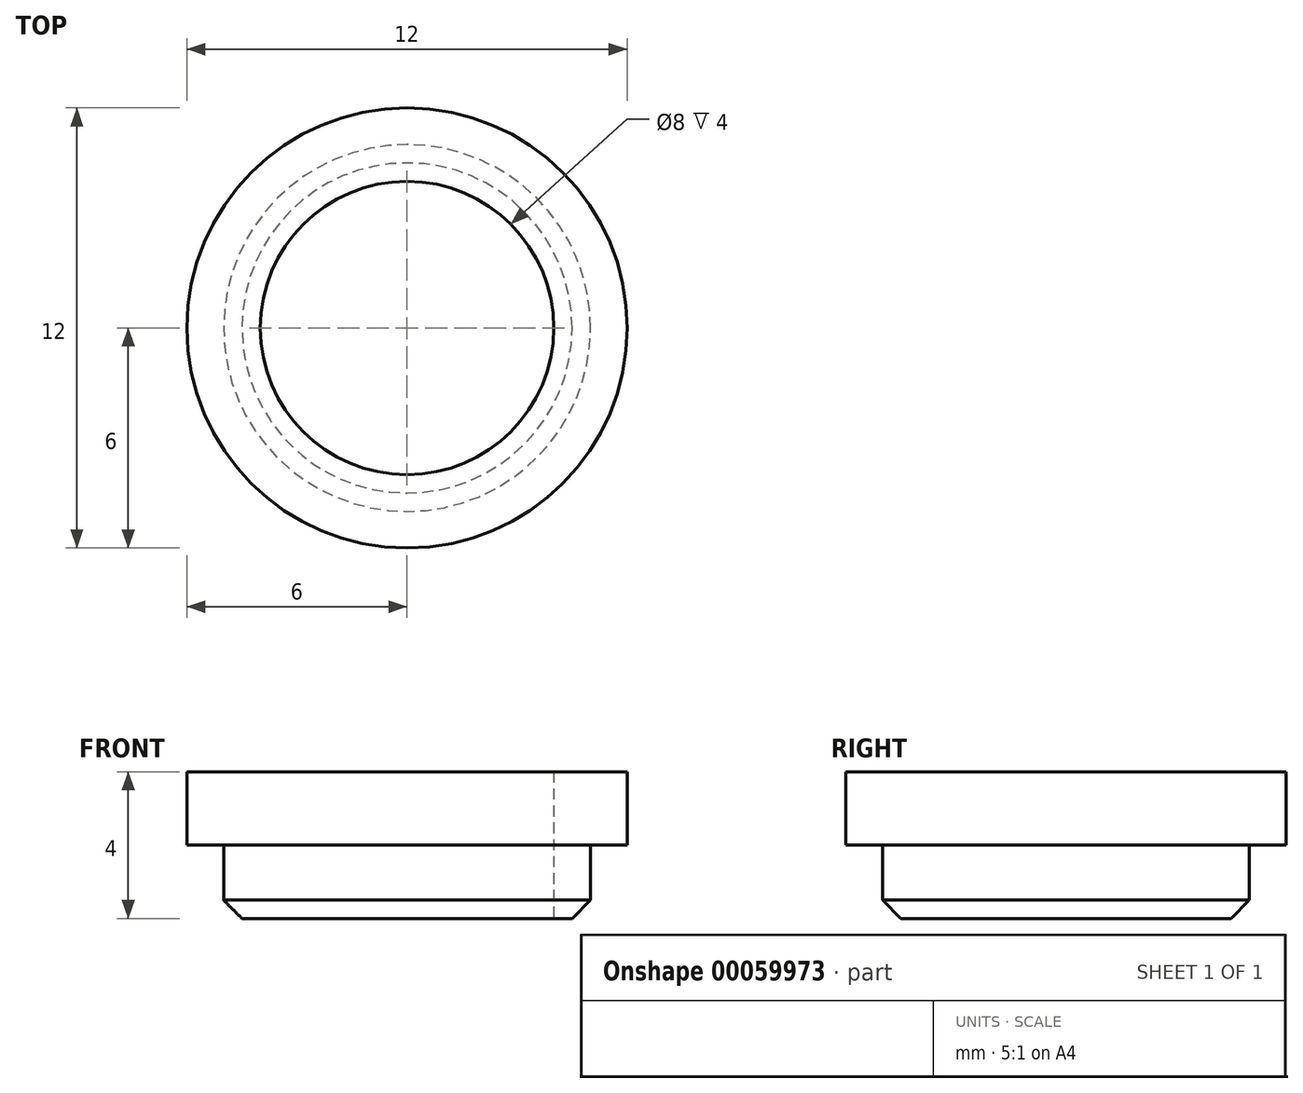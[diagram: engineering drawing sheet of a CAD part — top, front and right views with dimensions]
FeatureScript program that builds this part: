
annotation { "Feature Type Name" : "Feature", "Feature Type Description" : "" }
export const myFeature = defineFeature(function(context is Context, id is Id, definition is map)
    precondition{}
    {
        {
            var Q0;
            Q0=qCreatedBy(makeId("Top.planeOp"),FACE);
            var sketch = newSketch(context, id + "F0", { "sketchPlane" : qUnion([Q0])});
            skCircle(sketch, "E0", {"center": v(0, 0) * mm, "radius": 6 * mm});
            skCircle(sketch, "E1", {"center": v(0, 0) * mm, "radius": 4 * mm});
            skSolve(sketch);
        }
        {
            var Q0;
            Q0 = qSketchRegion(id + "F0", true);
            extrude(context, id + "F1", {"entities" : qUnion([Q0]), "depth" : 2 * mm});
        }
        {
            var Q0;
            Q0=makeQuery(id+"F1.opExtrude","CAP_FACE",FACE,{"disambiguationData":[OSD([sQuery(id+"F0.wireOp",EDGE,"E0"),sQuery(id+"F0.wireOp",EDGE,"E1")])],"isStart":true});
            var sketch = newSketch(context, id + "F2", { "sketchPlane" : qUnion([Q0])});
            skCircle(sketch, "E2.0", {"center": v(0, 0) * mm, "radius": 4 * mm});
            skCircle(sketch, "E3", {"center": v(0, 0) * mm, "radius": 5 * mm});
            skSolve(sketch);
        }
        {
            var Q0;
            Q0 = qSketchRegion(id + "F2", true);
            extrude(context, id + "F3", {"entities" : qUnion([Q0]), "operationType" : NewBodyOperationType.ADD, "depth" : 2 * mm});
        }
        {
            var Q0;
            Q0=makeQuery(id+"F3.opExtrude","CAP_EDGE",EDGE,{"disambiguationData":[OSD([sQuery(id+"F2.wireOp",EDGE,"E3")])],"isStart":false});
            chamfer(context, id + "F4", {"entities" : qUnion([Q0]), "width" : 0.5 * mm, "tangentPropagation" : true});
        }
    });
